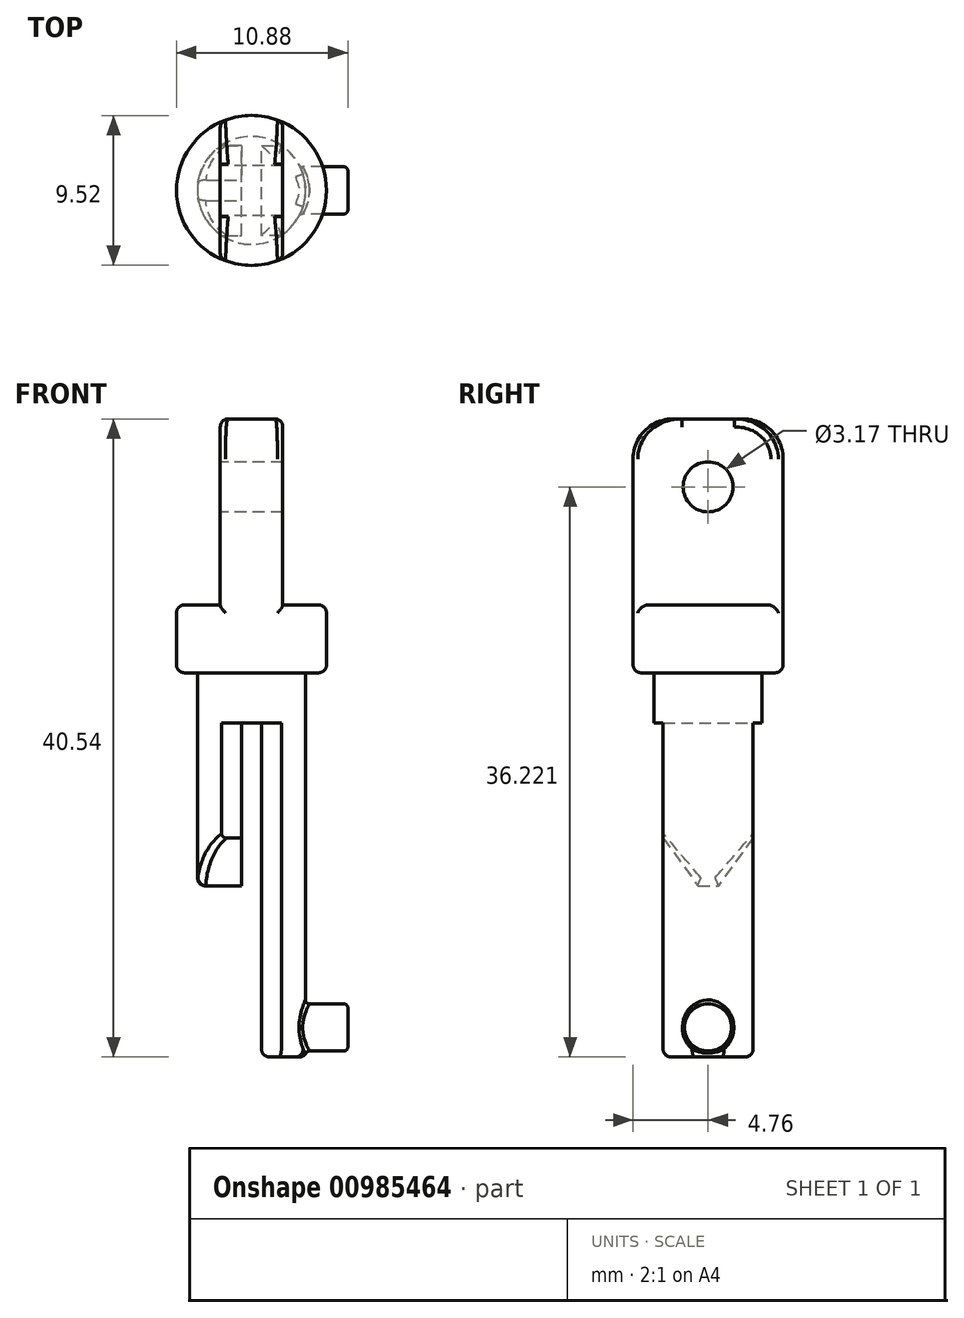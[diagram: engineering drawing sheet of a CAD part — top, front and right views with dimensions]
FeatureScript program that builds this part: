
annotation { "Feature Type Name" : "Feature", "Feature Type Description" : "" }
export const myFeature = defineFeature(function(context is Context, id is Id, definition is map)
    precondition{}
    {
        {
            var Q0;
            Q0=qCreatedBy(makeId("Top.planeOp"),FACE);
            var sketch = newSketch(context, id + "F0", { "sketchPlane" : qUnion([Q0])});
            skCircle(sketch, "E0", {"center": v(0, 0) * mm, "radius": 4.76 * mm});
            skSolve(sketch);
        }
        {
            var Q0;
            Q0 = qSketchRegion(id + "F0", true);
            extrude(context, id + "F1", {"entities" : qUnion([Q0]), "depth" : 4.32 * mm, "offsetDistance" : 25.4 * mm});
        }
        {
            var Q0;
            Q0=makeQuery(id+"F1.opExtrude","CAP_FACE",FACE,{"disambiguationData":[OSD([sQuery(id+"F0.wireOp",EDGE,"E0")])],"isStart":false});
            var sketch = newSketch(context, id + "F2", { "sketchPlane" : qUnion([Q0])});
            skLineSegment(sketch, "E1.left", {"start": v(-1.98, 4.33) * mm, "end": v(-1.98, -4.33) * mm});
            skLineSegment(sketch, "E1.right", {"start": v(1.98, 4.33) * mm, "end": v(1.98, -4.33) * mm});
            skArc(sketch, "E2", {"start": v(1.98, 4.33) * mm, "mid": v(0, 4.76) * mm, "end": v(-1.98, 4.33) * mm});
            skArc(sketch, "E3", {"start": v(-1.98, -4.33) * mm, "mid": v(0, -4.76) * mm, "end": v(1.98, -4.33) * mm});
            skSolve(sketch);
        }
        {
            var Q0;
            Q0 = qSketchRegion(id + "F2", true);
            extrude(context, id + "F3", {"entities" : qUnion([Q0]), "operationType" : NewBodyOperationType.ADD, "depth" : 11.8 * mm, "offsetDistance" : 25.4 * mm});
        }
        {
            var Q0;
            Q0=makeQuery(id+"F3.opExtrude","CAP_EDGE",EDGE,{"disambiguationData":[OSD([sQuery(id+"F2.wireOp",EDGE,"E3")])],"isStart":false});
            var Q1;
            Q1=makeQuery(id+"F3.opExtrude","CAP_EDGE",EDGE,{"disambiguationData":[OSD([sQuery(id+"F2.wireOp",EDGE,"E2")])],"isStart":false});
            fillet(context, id + "F4", {"entities" : qUnion([Q0, Q1]), "radius" : 2.54 * mm, "tangentPropagation" : true, "allowEdgeOverflow" : false});
        }
        {
            var Q0;
            Q0=makeQuery(id+"F1.opExtrude","CAP_FACE",FACE,{"disambiguationData":[OSD([sQuery(id+"F0.wireOp",EDGE,"E0")])],"isStart":true});
            var sketch = newSketch(context, id + "F5", { "sketchPlane" : qUnion([Q0])});
            skCircle(sketch, "E4", {"center": v(0, 0) * mm, "radius": 3.43 * mm});
            skSolve(sketch);
        }
        {
            var Q0;
            Q0 = qSketchRegion(id + "F5", true);
            extrude(context, id + "F6", {"entities" : qUnion([Q0]), "operationType" : NewBodyOperationType.ADD, "depth" : 3.17 * mm, "offsetDistance" : 25.4 * mm});
        }
        {
            var Q0;
            Q0=makeQuery(id+"F6.opExtrude","CAP_FACE",FACE,{"disambiguationData":[OSD([sQuery(id+"F5.wireOp",EDGE,"E4")])],"isStart":false});
            var sketch = newSketch(context, id + "F7", { "sketchPlane" : qUnion([Q0])});
            skLineSegment(sketch, "E5", {"start": v(-1.9, 2.86) * mm, "end": v(-0.63, 2.86) * mm});
            skLineSegment(sketch, "E6", {"start": v(-0.64, 2.86) * mm, "end": v(-0.63, -2.86) * mm});
            skLineSegment(sketch, "E7", {"start": v(-0.63, -2.86) * mm, "end": v(-1.9, -2.86) * mm});
            skArc(sketch, "E8", {"start": v(-1.9, 2.86) * mm, "mid": v(-3.43, 0) * mm, "end": v(-1.9, -2.86) * mm});
            skLineSegment(sketch, "E9.MirrorCS", {"start": v(1.9, 2.86) * mm, "end": v(0.63, 2.86) * mm});
            skArc(sketch, "E10.MirrorCS", {"start": v(1.9, 2.86) * mm, "mid": v(3.43, 0) * mm, "end": v(1.9, -2.86) * mm});
            skLineSegment(sketch, "E11.MirrorCS", {"start": v(0.64, 2.86) * mm, "end": v(0.63, -2.86) * mm});
            skLineSegment(sketch, "E12.MirrorCS", {"start": v(0.63, -2.86) * mm, "end": v(1.9, -2.86) * mm});
            skSolve(sketch);
        }
        {
            var Q0;
            Q0=makeQuery(id+"F7.imprint","IMPRINT",FACE,{"disambiguationData":[TD([[makeQuery(id+"F7.imprint","IMPRINT",EDGE,{"derivedFrom":sQuery(id+"F7.wireOp",EDGE,"E5")}),-1.0]])]});
            var Q1;
            Q1=makeQuery(id+"F7.imprint","IMPRINT",FACE,{"disambiguationData":[TD([[makeQuery(id+"F7.imprint","IMPRINT",EDGE,{"derivedFrom":sQuery(id+"F7.wireOp",EDGE,"E9.MirrorCS")}),1.0]])]});
            extrude(context, id + "F8", {"entities" : qUnion([Q0, Q1]), "operationType" : NewBodyOperationType.ADD, "depth" : 21.23 * mm, "offsetDistance" : 25.4 * mm});
        }
        {
            var Q0;
            Q0=qCreatedBy(makeId("Right.planeOp"),FACE);
            cPlane(context, id + "F9", {"entities" : qUnion([Q0]), "cplaneType" : CPlaneType.OFFSET, "offset" : 3.43 * mm, "width" : 152.4 * mm, "height" : 152.4 * mm});
        }
        {
            var Q0;
            Q0=qCreatedBy(id+"F9.planeOp",FACE);
            var sketch = newSketch(context, id + "F10", { "sketchPlane" : qUnion([Q0])});
            skCircle(sketch, "E13", {"center": v(0, -22.53) * mm, "radius": 1.5 * mm});
            skSolve(sketch);
        }
        {
            var Q0;
            Q0 = qSketchRegion(id + "F10", true);
            extrude(context, id + "F11", {"entities" : qUnion([Q0]), "operationType" : NewBodyOperationType.ADD, "depth" : 2.7 * mm, "offsetDistance" : 25.4 * mm, "hasSecondDirection" : true, "secondDirectionOppositeDirection" : true, "secondDirectionDepth" : 2.03 * mm});
        }
        {
            var Q0;
            Q0=makeQuery(id+"F11.opExtrude","CAP_EDGE",EDGE,{"disambiguationData":[OSD([sQuery(id+"F10.wireOp",EDGE,"E13")])],"isStart":false});
            fillet(context, id + "F12", {"entities" : qUnion([Q0]), "radius" : 0.25 * mm, "tangentPropagation" : true, "allowEdgeOverflow" : false});
        }
        {
            var Q0;
            Q0=makeQuery(id+"F11.boolean.opBoolean","INTERSECT",EDGE,{"derivedFrom":[makeQuery(id+"F8.boolean.opBoolean","MERGE",FACE,{"derivedFrom":[makeQuery(id+"F6.opExtrude","SWEPT_FACE",FACE,{"disambiguationData":[OSD([sQuery(id+"F5.wireOp",EDGE,"E4")])]}),makeQuery(id+"F8.opExtrude","SWEPT_FACE",FACE,{"disambiguationData":[OSD([sQuery(id+"F7.wireOp",EDGE,"E8")])]}),makeQuery(id+"F8.opExtrude","SWEPT_FACE",FACE,{"disambiguationData":[OSD([sQuery(id+"F7.wireOp",EDGE,"E10.MirrorCS")])]})]}),makeQuery(id+"F11.opExtrude","SWEPT_FACE",FACE,{"disambiguationData":[OSD([sQuery(id+"F10.wireOp",EDGE,"E13")])]})]});
            fillet(context, id + "F13", {"entities" : qUnion([Q0]), "radius" : 0.25 * mm, "tangentPropagation" : true, "allowEdgeOverflow" : false});
        }
        {
            var Q0;
            Q0=makeQuery(id+"F8.opExtrude","CAP_EDGE",EDGE,{"disambiguationData":[OSD([sQuery(id+"F7.wireOp",EDGE,"E10.MirrorCS")])],"isStart":false});
            var Q1;
            Q1=makeQuery(id+"F8.opExtrude","CAP_EDGE",EDGE,{"disambiguationData":[OSD([sQuery(id+"F7.wireOp",EDGE,"E12.MirrorCS")])],"isStart":false});
            var Q2;
            Q2=makeQuery(id+"F8.opExtrude","CAP_EDGE",EDGE,{"disambiguationData":[OSD([sQuery(id+"F7.wireOp",EDGE,"E7")])],"isStart":false});
            var Q3;
            Q3=makeQuery(id+"F8.opExtrude","CAP_EDGE",EDGE,{"disambiguationData":[OSD([sQuery(id+"F7.wireOp",EDGE,"E8")])],"isStart":false});
            var Q4;
            Q4=makeQuery(id+"F8.opExtrude","CAP_EDGE",EDGE,{"disambiguationData":[OSD([sQuery(id+"F7.wireOp",EDGE,"E5")])],"isStart":false});
            var Q5;
            Q5=makeQuery(id+"F8.opExtrude","CAP_EDGE",EDGE,{"disambiguationData":[OSD([sQuery(id+"F7.wireOp",EDGE,"E9.MirrorCS")])],"isStart":false});
            var Q6;
            Q6=makeQuery(id+"F8.opExtrude","CAP_EDGE",EDGE,{"disambiguationData":[OSD([sQuery(id+"F7.wireOp",EDGE,"E11.MirrorCS")])],"isStart":false});
            var Q7;
            Q7=makeQuery(id+"F8.opExtrude","CAP_EDGE",EDGE,{"disambiguationData":[OSD([sQuery(id+"F7.wireOp",EDGE,"E6")])],"isStart":false});
            fillet(context, id + "F14", {"entities" : qUnion([Q0, Q1, Q2, Q3, Q4, Q5, Q6, Q7]), "radius" : 0.5 * mm, "tangentPropagation" : true, "allowEdgeOverflow" : false});
        }
        {
            var Q0;
            {var subQ0=sQuery(id+"F0.wireOp",EDGE,"E0");Q0=makeQuery(id+"F3.boolean.opBoolean","SPLIT",EDGE,{"disambiguationData":[TD([makeQuery(id+"F3.opExtrude","SWEPT_FACE",FACE,{"disambiguationData":[OSD([sQuery(id+"F2.wireOp",EDGE,"E1.left")])]})])],"derivedFrom":makeQuery(id+"F1.opExtrude","CAP_EDGE",EDGE,{"disambiguationData":[OSD([subQ0])],"isStart":false})});}
            var Q1;
            {var subQ0=sQuery(id+"F0.wireOp",EDGE,"E0");Q1=makeQuery(id+"F3.boolean.opBoolean","SPLIT",EDGE,{"disambiguationData":[TD([makeQuery(id+"F3.opExtrude","SWEPT_FACE",FACE,{"disambiguationData":[OSD([sQuery(id+"F2.wireOp",EDGE,"E1.right")])]})])],"derivedFrom":makeQuery(id+"F1.opExtrude","CAP_EDGE",EDGE,{"disambiguationData":[OSD([subQ0])],"isStart":false})});}
            var Q2;
            Q2=makeQuery(id+"F3.opExtrude","SWEPT_EDGE",EDGE,{"disambiguationData":[OSD([sQuery(id+"F0.wireOp",EDGE,"E0"),sQuery(id+"F2.wireOp",EDGE,"E1.right"),sQuery(id+"F2.wireOp",EDGE,"E2")])]});
            var Q3;
            Q3=makeQuery(id+"F3.opExtrude","SWEPT_EDGE",EDGE,{"disambiguationData":[OSD([sQuery(id+"F0.wireOp",EDGE,"E0"),sQuery(id+"F2.wireOp",EDGE,"E1.left"),sQuery(id+"F2.wireOp",EDGE,"E2")])]});
            var Q4;
            Q4=makeQuery(id+"F1.opExtrude","CAP_EDGE",EDGE,{"disambiguationData":[OSD([sQuery(id+"F0.wireOp",EDGE,"E0")])],"isStart":true});
            var Q5;
            Q5=makeQuery(id+"F6.opExtrude","CAP_EDGE",EDGE,{"disambiguationData":[OSD([sQuery(id+"F5.wireOp",EDGE,"E4")])],"isStart":true});
            fillet(context, id + "F15", {"entities" : qUnion([Q0, Q1, Q2, Q3, Q4, Q5]), "radius" : 0.5 * mm, "tangentPropagation" : true, "allowEdgeOverflow" : false});
        }
        {
            var Q0;
            Q0=makeQuery(id+"F3.opExtrude","SWEPT_FACE",FACE,{"disambiguationData":[OSD([sQuery(id+"F2.wireOp",EDGE,"E1.left")])]});
            var sketch = newSketch(context, id + "F16", { "sketchPlane" : qUnion([Q0])});
            skCircle(sketch, "E14", {"center": v(0, 11.81) * mm, "radius": 1.59 * mm});
            skSolve(sketch);
        }
        {
            var Q0;
            Q0 = qSketchRegion(id + "F16", true);
            extrude(context, id + "F17", {"entities" : qUnion([Q0]), "operationType" : NewBodyOperationType.REMOVE, "endBound" : BoundingType.THROUGH_ALL, "oppositeDirection" : true, "depth" : 25.4 * mm, "offsetDistance" : 25.4 * mm});
        }
        {
            var Q0;
            Q0=makeQuery(id+"F8.opExtrude","SWEPT_FACE",FACE,{"disambiguationData":[OSD([sQuery(id+"F7.wireOp",EDGE,"E6")])]});
            var sketch = newSketch(context, id + "F18", { "sketchPlane" : qUnion([Q0])});
            skPoint(sketch, "E15.oppositeSnap0", {"position": v(2.86, -13.54) * mm});
            skLineSegment(sketch, "E15.bottom", {"start": v(-2.86, -13.54) * mm, "end": v(2.86, -13.54) * mm});
            skLineSegment(sketch, "E15.top", {"start": v(-2.86, -24.4) * mm, "end": v(2.86, -24.4) * mm});
            skLineSegment(sketch, "E15.left", {"start": v(-2.86, -13.54) * mm, "end": v(-2.86, -24.4) * mm});
            skLineSegment(sketch, "E15.right", {"start": v(2.86, -13.54) * mm, "end": v(2.86, -24.4) * mm});
            skSolve(sketch);
        }
        {
            var Q0;
            Q0 = qSketchRegion(id + "F18", true);
            extrude(context, id + "F19", {"entities" : qUnion([Q0]), "operationType" : NewBodyOperationType.REMOVE, "oppositeDirection" : true, "depth" : 25.4 * mm, "offsetDistance" : 25.4 * mm});
        }
        {
            var Q0;
            Q0=makeQuery(id+"F8.opExtrude","SWEPT_FACE",FACE,{"disambiguationData":[OSD([sQuery(id+"F7.wireOp",EDGE,"E6")])]});
            var sketch = newSketch(context, id + "F20", { "sketchPlane" : qUnion([Q0])});
            skLineSegment(sketch, "E16", {"start": v(-2.86, -10.48) * mm, "end": v(-0.64, -13.54) * mm});
            skLineSegment(sketch, "E17", {"start": v(-0.64, -13.54) * mm, "end": v(-2.86, -13.54) * mm});
            skLineSegment(sketch, "E18", {"start": v(-2.86, -13.54) * mm, "end": v(-2.86, -10.48) * mm});
            skLineSegment(sketch, "E19.MirrorCS", {"start": v(2.86, -10.48) * mm, "end": v(0.64, -13.54) * mm});
            skLineSegment(sketch, "E20.MirrorCS", {"start": v(2.86, -13.54) * mm, "end": v(2.86, -10.48) * mm});
            skLineSegment(sketch, "E21.MirrorCS", {"start": v(0.64, -13.54) * mm, "end": v(2.86, -13.54) * mm});
            skSolve(sketch);
        }
        {
            var Q0;
            Q0 = qSketchRegion(id + "F20", true);
            extrude(context, id + "F21", {"entities" : qUnion([Q0]), "operationType" : NewBodyOperationType.REMOVE, "oppositeDirection" : true, "depth" : 25.4 * mm, "offsetDistance" : 25.4 * mm});
        }
        {
            var Q0;
            Q0=makeQuery(id+"F21.boolean.opBoolean","COPY",EDGE,{"derivedFrom":makeQuery(id+"F21.opExtrude","CAP_EDGE",EDGE,{"disambiguationData":[OSD([sQuery(id+"F20.wireOp",EDGE,"E16")])],"isStart":true})});
            var Q1;
            Q1=makeQuery(id+"F19.boolean.opBoolean","COPY",EDGE,{"derivedFrom":makeQuery(id+"F19.opExtrude","CAP_EDGE",EDGE,{"disambiguationData":[OSD([sQuery(id+"F18.wireOp",EDGE,"E15.bottom")])],"isStart":true})});
            var Q2;
            Q2=makeQuery(id+"F21.boolean.opBoolean","COPY",EDGE,{"derivedFrom":makeQuery(id+"F21.opExtrude","CAP_EDGE",EDGE,{"disambiguationData":[OSD([sQuery(id+"F20.wireOp",EDGE,"E19.MirrorCS")])],"isStart":true})});
            var Q3;
            Q3=makeQuery(id+"F21.boolean.opBoolean","INTERSECT",EDGE,{"derivedFrom":[makeQuery(id+"F8.boolean.opBoolean","MERGE",FACE,{"derivedFrom":[makeQuery(id+"F6.opExtrude","SWEPT_FACE",FACE,{"disambiguationData":[OSD([sQuery(id+"F5.wireOp",EDGE,"E4")])]}),makeQuery(id+"F8.opExtrude","SWEPT_FACE",FACE,{"disambiguationData":[OSD([sQuery(id+"F7.wireOp",EDGE,"E8")])]}),makeQuery(id+"F8.opExtrude","SWEPT_FACE",FACE,{"disambiguationData":[OSD([sQuery(id+"F7.wireOp",EDGE,"E10.MirrorCS")])]})]}),makeQuery(id+"F21.opExtrude","SWEPT_FACE",FACE,{"disambiguationData":[OSD([sQuery(id+"F20.wireOp",EDGE,"E16")])]})]});
            var Q4;
            Q4=makeQuery(id+"F19.boolean.opBoolean","INTERSECT",EDGE,{"derivedFrom":[makeQuery(id+"F8.boolean.opBoolean","MERGE",FACE,{"derivedFrom":[makeQuery(id+"F6.opExtrude","SWEPT_FACE",FACE,{"disambiguationData":[OSD([sQuery(id+"F5.wireOp",EDGE,"E4")])]}),makeQuery(id+"F8.opExtrude","SWEPT_FACE",FACE,{"disambiguationData":[OSD([sQuery(id+"F7.wireOp",EDGE,"E8")])]}),makeQuery(id+"F8.opExtrude","SWEPT_FACE",FACE,{"disambiguationData":[OSD([sQuery(id+"F7.wireOp",EDGE,"E10.MirrorCS")])]})]}),makeQuery(id+"F19.opExtrude","SWEPT_FACE",FACE,{"disambiguationData":[OSD([sQuery(id+"F18.wireOp",EDGE,"E15.bottom")])]})]});
            var Q5;
            Q5=makeQuery(id+"F21.boolean.opBoolean","INTERSECT",EDGE,{"derivedFrom":[makeQuery(id+"F8.boolean.opBoolean","MERGE",FACE,{"derivedFrom":[makeQuery(id+"F6.opExtrude","SWEPT_FACE",FACE,{"disambiguationData":[OSD([sQuery(id+"F5.wireOp",EDGE,"E4")])]}),makeQuery(id+"F8.opExtrude","SWEPT_FACE",FACE,{"disambiguationData":[OSD([sQuery(id+"F7.wireOp",EDGE,"E8")])]}),makeQuery(id+"F8.opExtrude","SWEPT_FACE",FACE,{"disambiguationData":[OSD([sQuery(id+"F7.wireOp",EDGE,"E10.MirrorCS")])]})]}),makeQuery(id+"F21.opExtrude","SWEPT_FACE",FACE,{"disambiguationData":[OSD([sQuery(id+"F20.wireOp",EDGE,"E19.MirrorCS")])]})]});
            var Q6;
            Q6=makeQuery(id+"F21.boolean.opBoolean","COPY",EDGE,{"derivedFrom":makeQuery(id+"F21.opExtrude","SWEPT_EDGE",EDGE,{"disambiguationData":[OSD([sQuery(id+"F7.wireOp",EDGE,"E6"),sQuery(id+"F7.wireOp",EDGE,"E7"),sQuery(id+"F20.wireOp",EDGE,"E19.MirrorCS"),sQuery(id+"F20.wireOp",EDGE,"E20.MirrorCS")])]})});
            var Q7;
            Q7=makeQuery(id+"F21.boolean.opBoolean","COPY",EDGE,{"derivedFrom":makeQuery(id+"F21.opExtrude","SWEPT_EDGE",EDGE,{"disambiguationData":[OSD([sQuery(id+"F7.wireOp",EDGE,"E5"),sQuery(id+"F7.wireOp",EDGE,"E6"),sQuery(id+"F20.wireOp",EDGE,"E16"),sQuery(id+"F20.wireOp",EDGE,"E18")])]})});
            fillet(context, id + "F22", {"entities" : qUnion([Q0, Q1, Q2, Q3, Q4, Q5, Q6, Q7]), "radius" : 0.5 * mm, "tangentPropagation" : true, "allowEdgeOverflow" : false});
        }
    });
